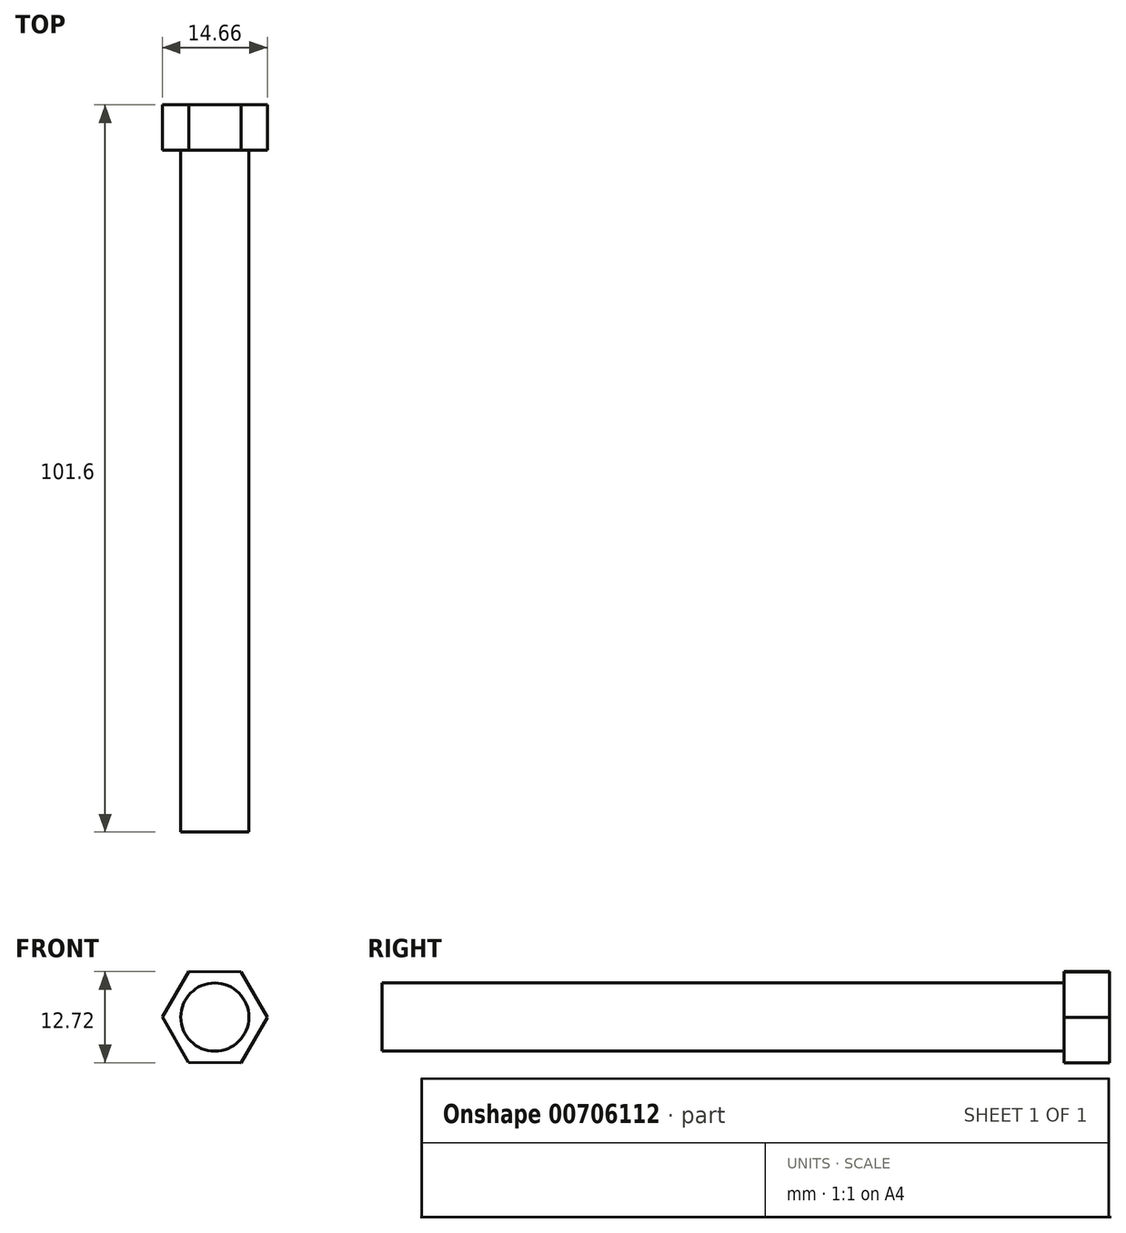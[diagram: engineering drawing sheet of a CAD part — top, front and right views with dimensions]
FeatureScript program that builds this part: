
annotation { "Feature Type Name" : "Feature", "Feature Type Description" : "" }
export const myFeature = defineFeature(function(context is Context, id is Id, definition is map)
    precondition{}
    {
        {
            var Q0;
            Q0=qCreatedBy(makeId("Front.planeOp"),FACE);
            var sketch = newSketch(context, id + "F0", { "sketchPlane" : qUnion([Q0])});
            skCircle(sketch, "E0", {"center": v(0, 0) * mm, "radius": 4.76 * mm});
            skSolve(sketch);
        }
        {
            var Q0;
            Q0=qSketchRegion(id+"F0",true);
            extrude(context, id + "F1", {"entities" : qUnion([Q0]), "depth" : 101.6 * mm, "offsetDistance" : 25.4 * mm});
        }
        {
            var Q0;
            Q0=qCreatedBy(makeId("Front.planeOp"),FACE);
            var sketch = newSketch(context, id + "F2", { "sketchPlane" : qUnion([Q0])});
            skCircle(sketch, "E1.cCircle", {"center": v(0, 0) * mm, "radius": 6.35 * mm, "construction": true});
            skLineSegment(sketch, "E1.0", {"start": v(3.68, 6.34) * mm, "end": v(7.33, -0.02) * mm});
            skLineSegment(sketch, "E1.1", {"start": v(7.33, -0.02) * mm, "end": v(3.65, -6.36) * mm});
            skLineSegment(sketch, "E1.2", {"start": v(3.65, -6.36) * mm, "end": v(-3.68, -6.34) * mm});
            skLineSegment(sketch, "E1.3", {"start": v(-3.68, -6.34) * mm, "end": v(-7.33, 0.02) * mm});
            skLineSegment(sketch, "E1.4", {"start": v(-7.33, 0.02) * mm, "end": v(-3.65, 6.36) * mm});
            skLineSegment(sketch, "E1.5", {"start": v(-3.65, 6.36) * mm, "end": v(3.68, 6.34) * mm});
            skPoint(sketch, "E1.0.midPoint", {"position": v(5.5, 3.16) * mm});
            skSolve(sketch);
        }
        {
            var Q0;
            Q0=qSketchRegion(id+"F2",true);
            extrude(context, id + "F3", {"entities" : qUnion([Q0]), "operationType" : NewBodyOperationType.ADD, "depth" : 6.35 * mm, "offsetDistance" : 25.4 * mm});
        }
    });
